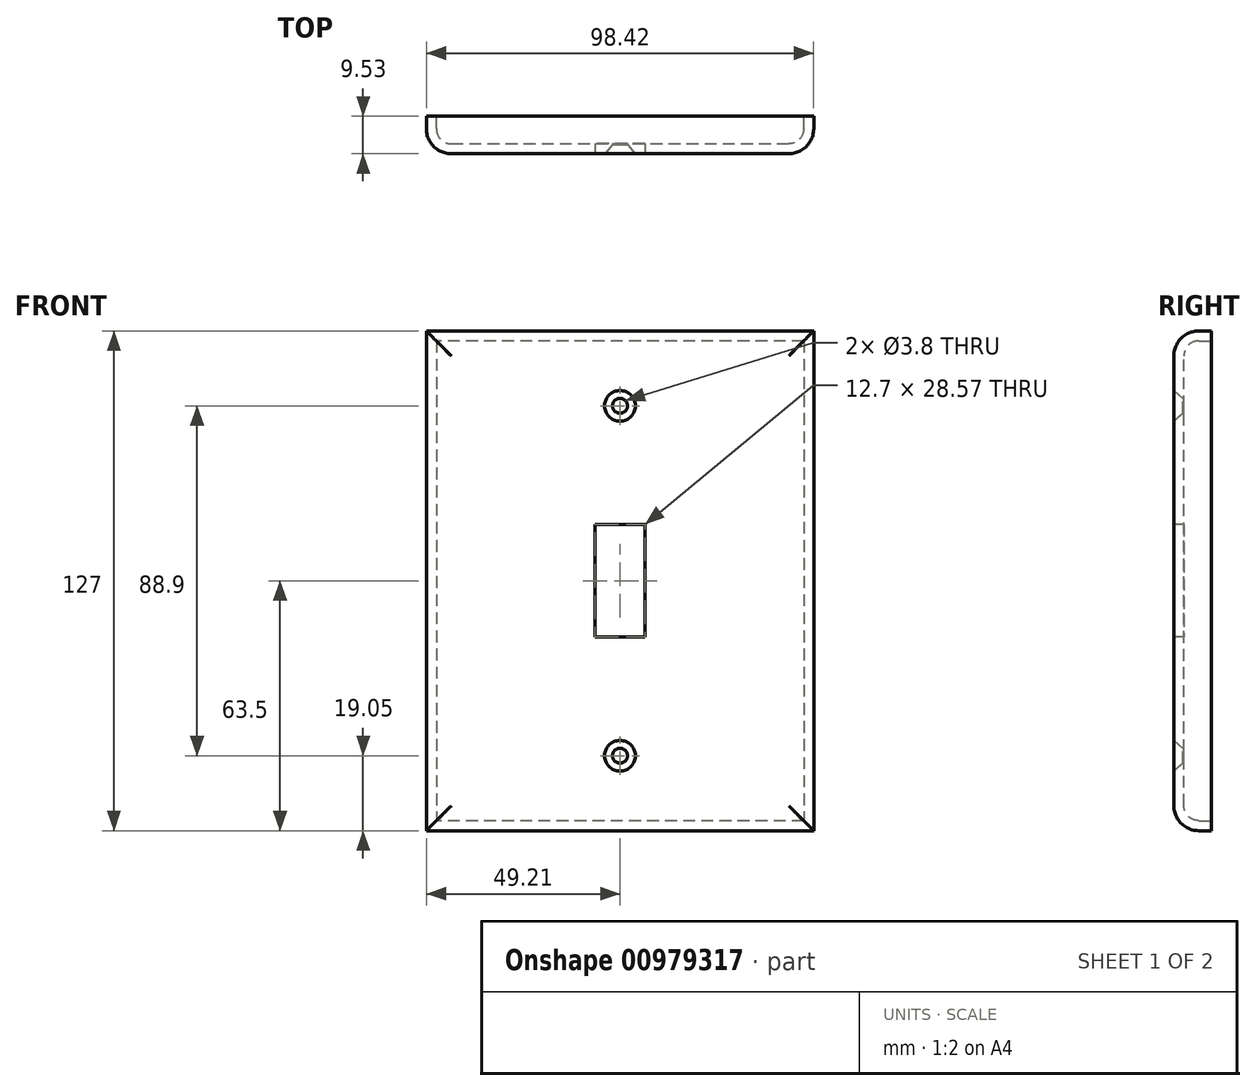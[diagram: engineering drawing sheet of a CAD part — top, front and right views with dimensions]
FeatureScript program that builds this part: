
annotation { "Feature Type Name" : "Feature", "Feature Type Description" : "" }
export const myFeature = defineFeature(function(context is Context, id is Id, definition is map)
    precondition{}
    {
        {
            var Q0;
            Q0=qCreatedBy(makeId("Front.planeOp"),FACE);
            var sketch = newSketch(context, id + "F0", { "sketchPlane" : qUnion([Q0])});
            skLineSegment(sketch, "E0.bottom", {"start": v(49.21, 63.5) * mm, "end": v(-49.21, 63.5) * mm});
            skLineSegment(sketch, "E0.top", {"start": v(49.21, -63.5) * mm, "end": v(-49.21, -63.5) * mm});
            skLineSegment(sketch, "E0.left", {"start": v(49.21, 63.5) * mm, "end": v(49.21, -63.5) * mm});
            skLineSegment(sketch, "E0.right", {"start": v(-49.21, 63.5) * mm, "end": v(-49.21, -63.5) * mm});
            skPoint(sketch, "E0.middle", {"position": v(0, 0) * mm});
            skSolve(sketch);
        }
        {
            var Q0;
            Q0=makeQuery(id+"F0.imprint","IMPRINT",FACE,{"disambiguationData":[TD([[makeQuery(id+"F0.imprint","IMPRINT",EDGE,{"derivedFrom":sQuery(id+"F0.wireOp",EDGE,"E0.bottom")}),1.0]])]});
            extrude(context, id + "F1", {"entities" : qUnion([Q0]), "depth" : 9.52 * mm, "offsetDistance" : 25.4 * mm});
        }
        {
            var Q0;
            Q0=makeQuery(id+"F1.opExtrude","CAP_FACE",FACE,{"disambiguationData":[OSD([sQuery(id+"F0.wireOp",EDGE,"E0.bottom"),sQuery(id+"F0.wireOp",EDGE,"E0.top"),sQuery(id+"F0.wireOp",EDGE,"E0.left"),sQuery(id+"F0.wireOp",EDGE,"E0.right")])],"isStart":false});
            fillet(context, id + "F2", {"entities" : qUnion([Q0]), "tangentPropagation" : true, "radius" : 6.35 * mm, "defaultsChanged" : false, "vertexSettings" : [], "allowEdgeOverflow" : false});
        }
        {
            var Q0;
            Q0=makeQuery(id+"F1.opExtrude","CAP_FACE",FACE,{"disambiguationData":[OSD([sQuery(id+"F0.wireOp",EDGE,"E0.bottom"),sQuery(id+"F0.wireOp",EDGE,"E0.top"),sQuery(id+"F0.wireOp",EDGE,"E0.left"),sQuery(id+"F0.wireOp",EDGE,"E0.right")])],"isStart":true});
            shell(context, id + "F3", {"entities" : qUnion([Q0]), "thickness" : 2.54 * mm});
        }
        {
            var Q0;
            Q0=makeQuery(id+"F1.opExtrude","CAP_FACE",FACE,{"disambiguationData":[OSD([sQuery(id+"F0.wireOp",EDGE,"E0.bottom"),sQuery(id+"F0.wireOp",EDGE,"E0.top"),sQuery(id+"F0.wireOp",EDGE,"E0.left"),sQuery(id+"F0.wireOp",EDGE,"E0.right")])],"isStart":false});
            var sketch = newSketch(context, id + "F4", { "sketchPlane" : qUnion([Q0])});
            skLineSegment(sketch, "E1.bottom", {"start": v(6.35, 14.29) * mm, "end": v(-6.35, 14.29) * mm});
            skLineSegment(sketch, "E1.top", {"start": v(6.35, -14.29) * mm, "end": v(-6.35, -14.29) * mm});
            skLineSegment(sketch, "E1.left", {"start": v(6.35, 14.29) * mm, "end": v(6.35, -14.29) * mm});
            skLineSegment(sketch, "E1.right", {"start": v(-6.35, 14.29) * mm, "end": v(-6.35, -14.29) * mm});
            skPoint(sketch, "E1.middle", {"position": v(0, 0) * mm});
            skPoint(sketch, "E2", {"position": v(0, 44.45) * mm});
            skLineSegment(sketch, "E3", {"start": v(-65.5, 0) * mm, "end": v(62.33, 0) * mm, "construction": true});
            skPoint(sketch, "E4.MirrorP", {"position": v(0, -44.45) * mm});
            skSolve(sketch);
        }
        {
            var Q0;
            Q0=makeQuery(id+"F4.imprint","IMPRINT",FACE,{"disambiguationData":[TD([[makeQuery(id+"F4.imprint","IMPRINT",EDGE,{"derivedFrom":sQuery(id+"F4.wireOp",EDGE,"E1.bottom")}),1.0]])]});
            extrude(context, id + "F5", {"entities" : qUnion([Q0]), "operationType" : NewBodyOperationType.REMOVE, "endBound" : BoundingType.THROUGH_ALL, "oppositeDirection" : true, "depth" : 25.4 * mm, "offsetDistance" : 25.4 * mm});
        }
        {
            var Q0;
            Q0=sQuery(id+"F4.wireOp",VERTEX,"E2");
            var Q1;
            Q1=sQuery(id+"F4.wireOp",VERTEX,"E4.MirrorP");
            var Q2;
            Q2=makeQuery(id+"F1.opExtrude","SWEPT_BODY",BODY,{"disambiguationData":[OSD([sQuery(id+"F0.wireOp",EDGE,"E0.bottom"),sQuery(id+"F0.wireOp",EDGE,"E0.top"),sQuery(id+"F0.wireOp",EDGE,"E0.left"),sQuery(id+"F0.wireOp",EDGE,"E0.right")])]});
            hole(context, id + "F6", {"style" : HoleStyle.C_SINK, "endStyle" : HoleEndStyle.BLIND, "standardTappedOrClearance" : lookupTablePath({ "fit" : "Free", "standard" : "ANSI", "size" : "#6", "type" : "Clearance" }), "standardBlindInLast" : lookupTablePath({ "fit" : "Free", "standard" : "ANSI", "engagement" : "75%", "pitch" : "32 tpi", "size" : "#6", "type" : "Clearance & tapped" }), "holeDiameter" : 3.8 * mm, "cSinkDiameter" : 7.8 * mm, "cSinkAngle" : 82 * degree, "majorDiameter" : 6.35 * mm, "holeDepth" : 12.7 * mm, "isTappedThrough" : true, "tappedDepth" : 12.7 * mm, "tapClearance" : 3, "startFromSketch" : true, "locations" : qUnion([Q0, Q1]), "scope" : qUnion([Q2])});
        }
    });
